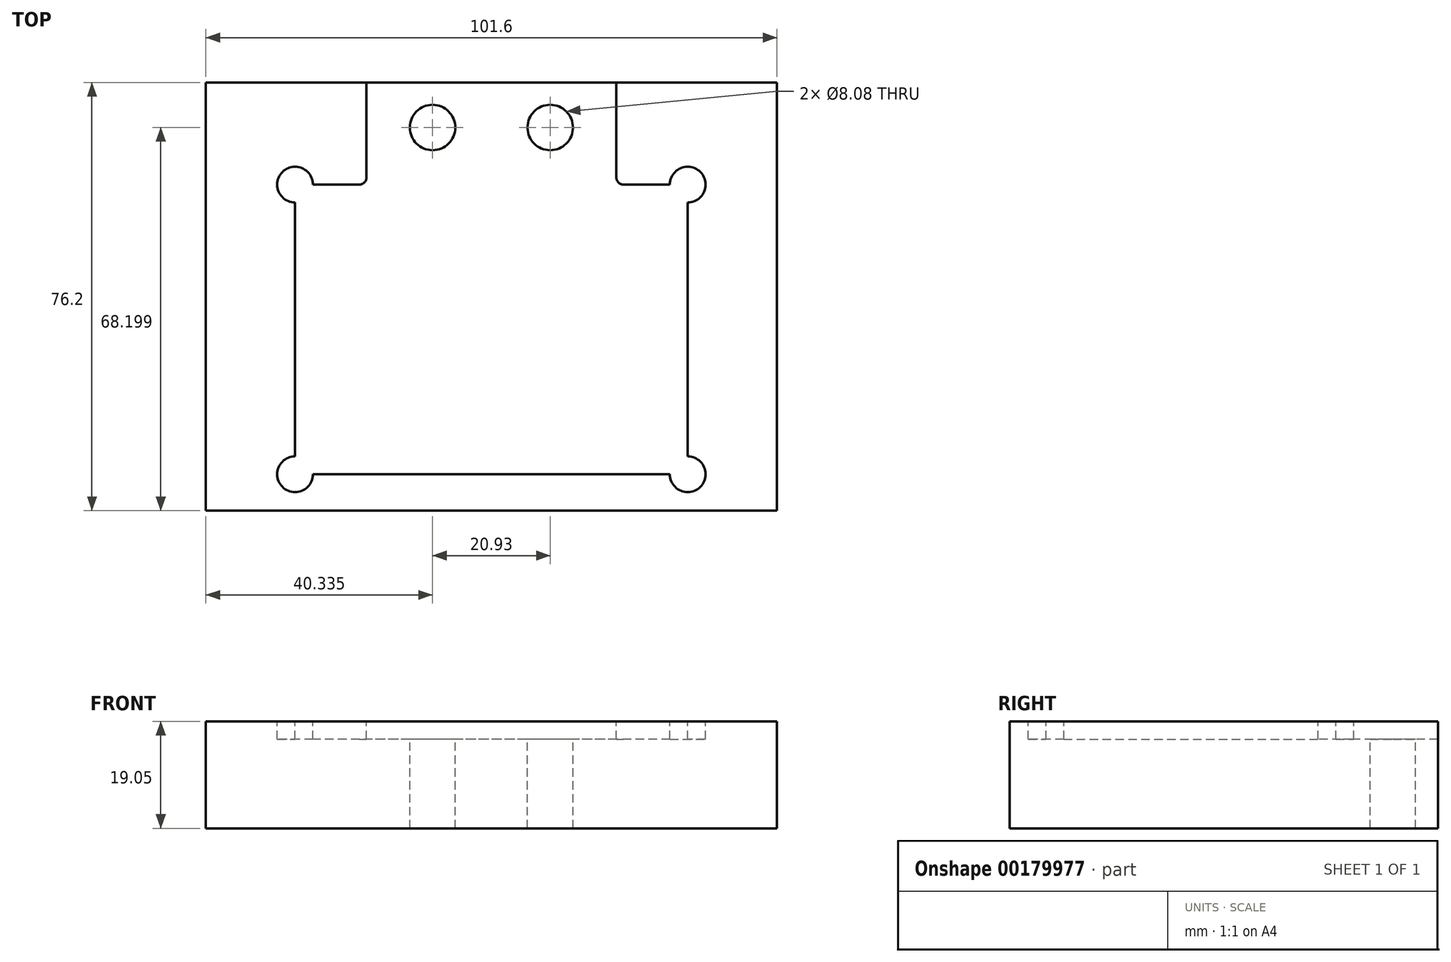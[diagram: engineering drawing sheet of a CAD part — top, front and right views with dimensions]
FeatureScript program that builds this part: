
annotation { "Feature Type Name" : "Feature", "Feature Type Description" : "" }
export const myFeature = defineFeature(function(context is Context, id is Id, definition is map)
    precondition{}
    {
        {
            var Q0;
            Q0=qCreatedBy(makeId("Top.planeOp"),FACE);
            var sketch = newSketch(context, id + "F0", { "sketchPlane" : qUnion([Q0])});
            skLineSegment(sketch, "E0.bottom", {"start": v(50.8, -38.1) * mm, "end": v(20.62, -38.1) * mm});
            skLineSegment(sketch, "E0.top", {"start": v(50.8, 38.1) * mm, "end": v(-50.8, 38.1) * mm});
            skLineSegment(sketch, "E0.left", {"start": v(50.8, -38.1) * mm, "end": v(50.8, 38.1) * mm});
            skLineSegment(sketch, "E0.right", {"start": v(-50.8, -38.1) * mm, "end": v(-50.8, 38.1) * mm});
            skPoint(sketch, "E0.middle", {"position": v(0, 0) * mm});
            skLineSegment(sketch, "E1.bottom", {"start": v(31.75, -31.62) * mm, "end": v(-31.75, -31.62) * mm});
            skLineSegment(sketch, "E1.top", {"start": v(31.75, 19.94) * mm, "end": v(23.5, 19.94) * mm});
            skLineSegment(sketch, "E1.left", {"start": v(34.93, -28.45) * mm, "end": v(34.93, 16.76) * mm});
            skLineSegment(sketch, "E1.right", {"start": v(-34.93, -28.45) * mm, "end": v(-34.93, 16.76) * mm});
            skArc(sketch, "E2", {"start": v(34.93, 16.76) * mm, "mid": v(37.17, 22.18) * mm, "end": v(31.75, 19.94) * mm});
            skArc(sketch, "E3", {"start": v(31.75, -31.62) * mm, "mid": v(37.17, -33.87) * mm, "end": v(34.93, -28.45) * mm});
            skArc(sketch, "E4", {"start": v(-34.93, -28.45) * mm, "mid": v(-37.17, -33.87) * mm, "end": v(-31.75, -31.62) * mm});
            skArc(sketch, "E5", {"start": v(-31.75, 19.94) * mm, "mid": v(-37.17, 22.18) * mm, "end": v(-34.93, 16.76) * mm});
            skLineSegment(sketch, "E6.top", {"start": v(20.62, -38.1) * mm, "end": v(-20.62, -38.1) * mm});
            skLineSegment(sketch, "E7.trimOffspring", {"start": v(-20.62, -38.1) * mm, "end": v(-50.8, -38.1) * mm});
            skLineSegment(sketch, "E8.trimOffspring", {"start": v(-23.5, 19.94) * mm, "end": v(-31.75, 19.94) * mm});
            skPoint(sketch, "E9.visualSharp", {"position": v(-20.62, 25.78) * mm});
            skPoint(sketch, "E10.visualSharp", {"position": v(20.62, 25.78) * mm});
            skLineSegment(sketch, "E11", {"start": v(22.23, 40.98) * mm, "end": v(0, 40.98) * mm});
            skLineSegment(sketch, "E12", {"start": v(0, 40.98) * mm, "end": v(-22.23, 40.98) * mm});
            skLineSegment(sketch, "E13", {"start": v(-22.23, 40.98) * mm, "end": v(-22.23, 21.2) * mm});
            skLineSegment(sketch, "E14", {"start": v(22.23, 40.98) * mm, "end": v(22.23, 21.2) * mm});
            skPoint(sketch, "E15.orphan", {"position": v(-21.9, 39.55) * mm});
            skPoint(sketch, "E16.start.orphan", {"position": v(0, 39.55) * mm});
            skPoint(sketch, "E17.start.orphan", {"position": v(20.62, 38.1) * mm});
            skPoint(sketch, "E18.start.orphan", {"position": v(21.9, 39.55) * mm});
            skPoint(sketch, "E19.orphan", {"position": v(20.62, 32.26) * mm});
            skPoint(sketch, "E10.filletArc.center.orphan", {"position": v(21.9, 21.2) * mm});
            skPoint(sketch, "E20.orphan", {"position": v(21.9, 19.94) * mm});
            skPoint(sketch, "E21.visualSharp", {"position": v(22.23, 19.94) * mm});
            skArc(sketch, "E21.filletArc", {"start": v(22.23, 21.2) * mm, "mid": v(22.6, 20.31) * mm, "end": v(23.5, 19.94) * mm});
            skPoint(sketch, "E22.visualSharp", {"position": v(-22.23, 19.94) * mm});
            skArc(sketch, "E22.filletArc", {"start": v(-23.5, 19.94) * mm, "mid": v(-22.6, 20.31) * mm, "end": v(-22.23, 21.2) * mm});
            skSolve(sketch);
        }
        {
            var Q0;
            Q0=makeQuery(id+"F0.imprint","IMPRINT",FACE,{"disambiguationData":[TD([[makeQuery(id+"F0.imprint","IMPRINT",EDGE,{"derivedFrom":sQuery(id+"F0.wireOp",EDGE,"E0.bottom")}),-1.0]])]});
            var Q1;
            Q1=makeQuery(id+"F0.imprint","IMPRINT",FACE,{"disambiguationData":[TD([[makeQuery(id+"F0.imprint","IMPRINT",EDGE,{"derivedFrom":sQuery(id+"F0.wireOp",EDGE,"E1.bottom")}),-1.0]])]});
            extrude(context, id + "F1", {"entities" : qUnion([Q0, Q1]), "oppositeDirection" : true, "depth" : 19.05 * mm});
        }
        {
            var Q0;
            Q0=makeQuery(id+"F0.imprint","IMPRINT",FACE,{"disambiguationData":[TD([[makeQuery(id+"F0.imprint","IMPRINT",EDGE,{"derivedFrom":sQuery(id+"F0.wireOp",EDGE,"E1.bottom")}),-1.0]])]});
            extrude(context, id + "F2", {"entities" : qUnion([Q0]), "operationType" : NewBodyOperationType.REMOVE, "oppositeDirection" : true, "depth" : 3.17 * mm});
        }
        {
            var Q0;
            Q0=makeQuery(id+"F2.boolean.opBoolean","COPY",FACE,{"derivedFrom":makeQuery(id+"F2.opExtrude","CAP_FACE",FACE,{"disambiguationData":[OSD([sQuery(id+"F0.wireOp",EDGE,"E0.top"),sQuery(id+"F0.wireOp",EDGE,"E1.bottom"),sQuery(id+"F0.wireOp",EDGE,"E1.top"),sQuery(id+"F0.wireOp",EDGE,"E1.left"),sQuery(id+"F0.wireOp",EDGE,"E1.right"),sQuery(id+"F0.wireOp",EDGE,"E2"),sQuery(id+"F0.wireOp",EDGE,"E3"),sQuery(id+"F0.wireOp",EDGE,"E4"),sQuery(id+"F0.wireOp",EDGE,"E5"),sQuery(id+"F0.wireOp",EDGE,"E8.trimOffspring"),sQuery(id+"F0.wireOp",EDGE,"E13"),sQuery(id+"F0.wireOp",EDGE,"E14"),sQuery(id+"F0.wireOp",EDGE,"E21.filletArc"),sQuery(id+"F0.wireOp",EDGE,"E22.filletArc")])],"isStart":false})});
            var sketch = newSketch(context, id + "F3", { "sketchPlane" : qUnion([Q0])});
            skLineSegment(sketch, "E23", {"start": v(-23.5, 19.94) * mm, "end": v(23.5, 19.94) * mm});
            skLineSegment(sketch, "E24", {"start": v(0, 19.94) * mm, "end": v(0, 30.1) * mm});
            skPoint(sketch, "E24.endSnap0", {"position": v(0, 19.94) * mm});
            skLineSegment(sketch, "E25", {"start": v(0, 30.1) * mm, "end": v(10.46, 30.1) * mm});
            skLineSegment(sketch, "E26", {"start": v(0, 30.1) * mm, "end": v(-10.46, 30.1) * mm});
            skCircle(sketch, "E27", {"center": v(-10.46, 30.1) * mm, "radius": 4.04 * mm});
            skCircle(sketch, "E28", {"center": v(10.46, 30.1) * mm, "radius": 4.04 * mm});
            skSolve(sketch);
        }
        {
            var Q0;
            Q0 = qSketchRegion(id + "F3", true);
            extrude(context, id + "F4", {"entities" : qUnion([Q0]), "operationType" : NewBodyOperationType.REMOVE, "oppositeDirection" : true, "depth" : 25.4 * mm});
        }
    });
